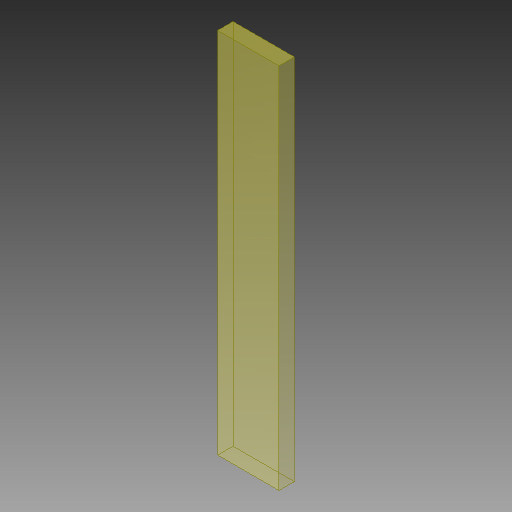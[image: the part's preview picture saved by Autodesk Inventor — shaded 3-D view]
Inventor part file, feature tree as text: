
AUTODESK INVENTOR PART (.ipt)
format: ipt  version: 2018.1 (Build 221171000, 171)  size: 90,624 bytes
history: native  units: mm
features: other x1, extrude x1, sketch x1
ambient origin geometry x8: Origin, YZ Plane, XZ Plane, XY Plane, X Axis, Y Axis, Z Axis, Center Point
bodies: Solid1 (feature_tree)
feature tree (3):
  parser-record x1  (decoder bookkeeping rows leaked as tree rows — omitted from the tree; the rows remain in map.json)
  extrude  "Extrusion1"  Depth=120.0mm
  sketch  "Sketch1"  dims[d0=20.0mm d1=120.0mm d2=5.0mm d3=0.0mm]
note: 1 file-system path scrubbed to <path> (originals preserved in map.json)
